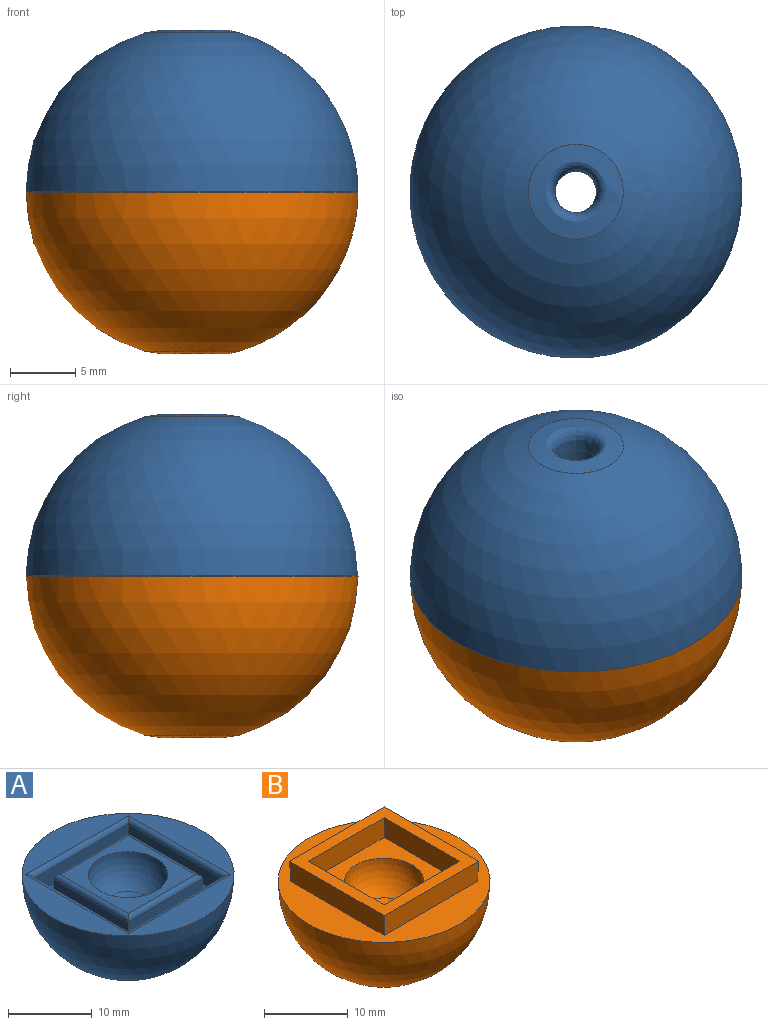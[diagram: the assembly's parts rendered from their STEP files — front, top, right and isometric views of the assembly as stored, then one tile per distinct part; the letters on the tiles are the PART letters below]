
ASSEMBLY  parts=2 mates=1
PART A: 24 faces, bbox 25.4x25.4x12.5 mm
  f0: sphere r=12.7mm, area 971.2mm2, adj f2,f14
  f1: sphere r=4.76mm, area 123.4mm2, adj f12,f15
  f2: plane 25.4x25.4mm, normal (0,0,1), area 207.6mm2, adj f0,f20,f21,f22,f23
  f3: plane 12.68x2.53mm, normal (0,1,-0.02), area 32mm2, adj f4,f10,f11,f16
  f4: plane 12.68x2.53mm, normal (1,0,-0.02), area 32mm2, adj f3,f5,f11,f17
  f5: plane 12.68x2.53mm, normal (0,-1,-0.02), area 32mm2, adj f4,f10,f11,f19
  f6: plane 16.11x2.53mm, normal (0,1,-0.02), area 40.6mm2, adj f7,f9,f11,f21
  f7: plane 16.11x2.53mm, normal (-1,0,-0.02), area 40.6mm2, adj f6,f8,f11,f20
  f8: plane 16.11x2.53mm, normal (0,-1,-0.02), area 40.6mm2, adj f7,f9,f11,f22
  f9: plane 16.11x2.53mm, normal (1,0,-0.02), area 40.6mm2, adj f6,f8,f11,f23
  f10: plane 12.68x2.53mm, normal (-1,0,-0.02), area 32mm2, adj f3,f5,f11,f18
  f11: plane 16.11x16.11mm, normal (0,0,1), area 101.1mm2, adj f3,f4,f5,f6,f7,f8,f9,f10
  f12: plane 11.41x11.41mm, normal (0,0,1), area 58.9mm2, adj f1,f16,f17,f18,f19
  f13: cylinder r=1.59mm len=5.15mm, axis (0,0,-1), area 51.4mm2, adj f14,f15
  f14: bspline ~8.04x8.04mm, area 47.6mm2, adj f0,f13
  f15: bspline ~4.76x4.76mm, area 20mm2, adj f1,f13
  f16: cylinder r=0.64mm len=12.68mm, axis (1,0,0), area 12.1mm2, adj f3,f12,f17,f18
  f17: cylinder r=0.64mm len=12.68mm, axis (0,1,0), area 12.1mm2, adj f4,f12,f16,f19
  f18: cylinder r=0.64mm len=12.68mm, axis (0,1,0), area 12.1mm2, adj f10,f12,f16,f19
  f19: cylinder r=0.64mm len=12.68mm, axis (1,0,0), area 12.1mm2, adj f5,f12,f17,f18
  f20: cylinder r=0.64mm len=17.29mm, axis (0,-1,0), area 16.8mm2, adj f2,f7,f21,f22
  f21: cylinder r=0.64mm len=17.29mm, axis (1,0,0), area 16.8mm2, adj f2,f6,f20,f23
  f22: cylinder r=0.64mm len=17.29mm, axis (1,0,0), area 16.8mm2, adj f2,f8,f20,f23
  f23: cylinder r=0.64mm len=17.29mm, axis (0,-1,0), area 16.8mm2, adj f2,f9,f21,f22
PART B: 16 faces, bbox 25.4x25.4x15.4 mm
  f0: sphere r=12.7mm, area 971.2mm2, adj f2,f14
  f1: sphere r=4.76mm, area 123.4mm2, adj f12,f15
  f2: plane 25.4x25.4mm, normal (0,0,1), area 254.7mm2, adj f0,f6,f7,f8,f9
  f3: plane 12.83x2.92mm, normal (0,-1,-0.01), area 37.4mm2, adj f4,f10,f11,f12
  f4: plane 12.83x2.92mm, normal (-1,0,-0.01), area 37.4mm2, adj f3,f5,f11,f12
  f5: plane 12.83x2.92mm, normal (0,1,-0.01), area 37.4mm2, adj f4,f10,f11,f12
  f6: plane 15.95x2.92mm, normal (0,-1,-0.01), area 46.5mm2, adj f2,f7,f9,f11
  f7: plane 15.95x2.92mm, normal (1,0,-0.01), area 46.5mm2, adj f2,f6,f8,f11
  f8: plane 15.95x2.92mm, normal (0,1,-0.01), area 46.5mm2, adj f2,f7,f9,f11
  f9: plane 15.95x2.92mm, normal (-1,0,-0.01), area 46.5mm2, adj f2,f6,f8,f11
  f10: plane 12.83x2.92mm, normal (1,0,-0.01), area 37.4mm2, adj f3,f5,f11,f12
  f11: plane 15.95x15.95mm, normal (0,0,1), area 91.9mm2, adj f3,f4,f5,f6,f7,f8,f9,f10
  f12: plane 12.83x12.83mm, normal (0,0,1), area 93.3mm2, adj f1,f3,f4,f5,f10
  f13: cylinder r=1.59mm len=5.15mm, axis (0,0,-1), area 51.4mm2, adj f14,f15
  f14: bspline ~8.04x8.04mm, area 47.6mm2, adj f0,f13
  f15: bspline ~4.76x4.76mm, area 20mm2, adj f1,f13
PLACE A rot(axis=(1,0,0),180deg) t=(-13.82,4.42,43.99)mm
PLACE B t=(-13.82,4.42,18.59)mm
MATE fastened A.f13 <-> B.f13  axis (0,0,-1) through (-13.82,4.42,31.29)mm
